# Revit family: ASSA_ABLOY_SW60
name_source: partatom
category: Specialty Equipment
units: mm (PartAtom-declared; Revit-internal decimal feet)

## family parameters
Always vertical = No
Cut with Voids When Loaded = No
Part Type = Normal
Room Calculation Point = No
Round Connector Dimension = Use Diameter
Shared = No
Work Plane-Based = Yes

## types (2) — shared parameters
Arm Height = 0' - 0 7/8"
Assembly Code = C1020410
CapDepth = 0' - 0 3/16"
Default Elevation = 4' - 0"
Depth = 0' - 2 3/8"
End Cap Finish = Black Plastic
Height = 0' - 1 7/8"
Housing Finish = Anodized Aluminum
Keynote = 07 81 00
Manufacturer = Assa Abloy
Pivot Location From Hinge = 0' - 9 1/2"
SpindleLoc = 0' - 9 1/2"
URL = https://www.assaabloyentrance.com
Width = 3' - 3 1/2"

## per-type parameters (varying)
| type | Arm Depth | Description | Model | PivotLocH | Spindle1Depth | Spindle2Depth |
| Pull Application | 0' - 1 1/4" | Assa Abloy SW60 Door Operator - Pull Application | SW60 - Pull Application | 0' - 10 11/16" | 0' - 0 1/4" | 0' - 0 15/32" |
| Push Application | 0' - 1" | Assa Abloy SW60 Door Operator - Push Application | SW60 - Push Application | 0' - 2 5/8" | 0' - 0 1/2" | 0' - 1" |

type visibility flags: 2 boolean params named "<type name>" — each type sets only its own to Yes (folded from table)

## geometry (parser evidence)
native form markers: Sweep x2
no freeform markers — native parametric forms only
